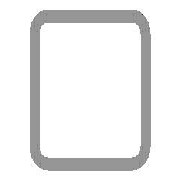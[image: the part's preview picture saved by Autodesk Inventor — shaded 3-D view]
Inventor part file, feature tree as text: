
AUTODESK INVENTOR PART (.ipt)
format: ipt  version: 2025.3 (Build 293356030, 356C)  size: 130,560 bytes
history: native  units: mm (DEFAULTED — no unit token found)
features: other x3, sketch x1, plane x1
ambient origin geometry x8: Origin, YZ Plane, XZ Plane, XY Plane, X Axis, Y Axis, Z Axis, Center Point
bodies: Solid1 (feature_tree), Body (feature_tree)
feature tree (5):
  other  "Driven Length"
  other  "Start plane"
  other  "End plane"
  sketch  "Sketch3"  dims[d3=2200.0mm d4=0.0mm d7=6.0mm d9=80.0mm d11=80.0mm d12=3.0mm d13=-0.0mm d14=2200.0mm d15=40.0mm d16=40.0mm d17=90.0deg d18=2200.0mm]
  plane  "Work Plane3"
